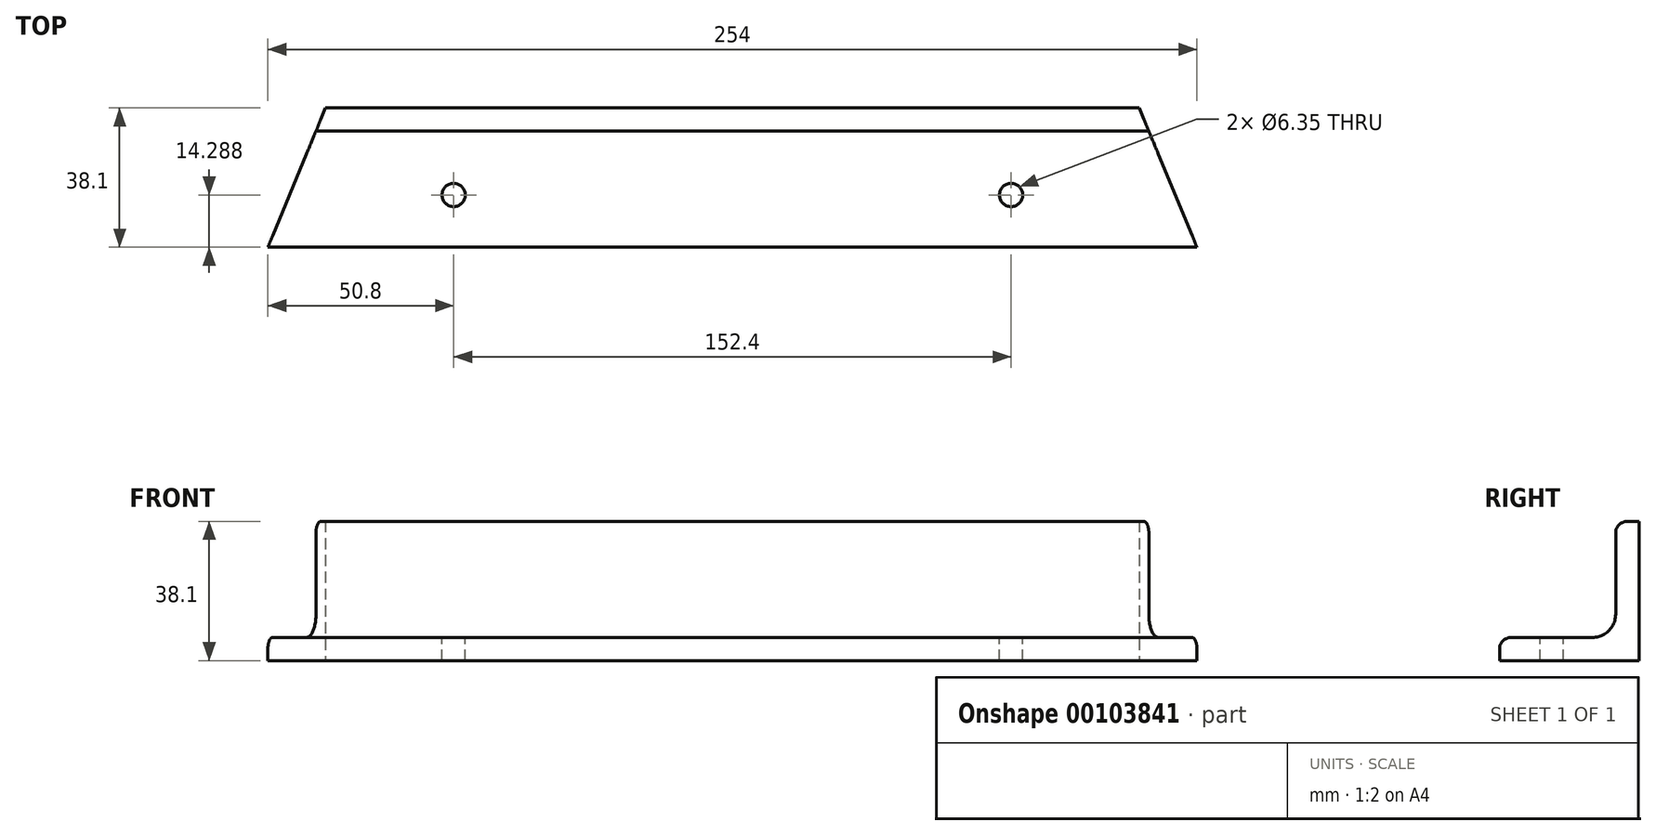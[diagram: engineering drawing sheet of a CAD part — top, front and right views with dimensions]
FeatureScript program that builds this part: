
annotation { "Feature Type Name" : "Feature", "Feature Type Description" : "" }
export const myFeature = defineFeature(function(context is Context, id is Id, definition is map)
    precondition{}
    {
        {
            var Q0;
            Q0=qCreatedBy(makeId("Right.planeOp"),FACE);
            var sketch = newSketch(context, id + "F0", { "sketchPlane" : qUnion([Q0])});
            skLineSegment(sketch, "E0", {"start": v(0, 0) * mm, "end": v(0, 38.1) * mm});
            skLineSegment(sketch, "E1", {"start": v(0, 38.1) * mm, "end": v(-6.35, 38.1) * mm});
            skLineSegment(sketch, "E2", {"start": v(-6.35, 38.1) * mm, "end": v(-6.35, 6.35) * mm});
            skLineSegment(sketch, "E3", {"start": v(-6.35, 6.35) * mm, "end": v(-38.1, 6.35) * mm});
            skLineSegment(sketch, "E4", {"start": v(-38.1, 6.35) * mm, "end": v(-38.1, 0) * mm});
            skLineSegment(sketch, "E5", {"start": v(-38.1, 0) * mm, "end": v(0, 0) * mm});
            skSolve(sketch);
        }
        {
            var Q0;
            Q0 = qSketchRegion(id + "F0", true);
            extrude(context, id + "F1", {"entities" : qUnion([Q0]), "endBound" : BoundingType.SYMMETRIC, "depth" : 254 * mm});
        }
        {
            var Q0;
            Q0=makeQuery(id+"F1.opExtrude","SWEPT_EDGE",EDGE,{"disambiguationData":[OSD([sQuery(id+"F0.wireOp",EDGE,"E2"),sQuery(id+"F0.wireOp",EDGE,"E3")])]});
            fillet(context, id + "F2", {"entities" : qUnion([Q0]), "radius" : 6.35 * mm, "tangentPropagation" : true, "allowEdgeOverflow" : false});
        }
        {
            var Q0;
            Q0=makeQuery(id+"F1.opExtrude","SWEPT_EDGE",EDGE,{"disambiguationData":[OSD([sQuery(id+"F0.wireOp",EDGE,"E1"),sQuery(id+"F0.wireOp",EDGE,"E2")])]});
            var Q1;
            Q1=makeQuery(id+"F1.opExtrude","SWEPT_EDGE",EDGE,{"disambiguationData":[OSD([sQuery(id+"F0.wireOp",EDGE,"E3"),sQuery(id+"F0.wireOp",EDGE,"E4")])]});
            fillet(context, id + "F3", {"entities" : qUnion([Q0, Q1]), "radius" : 3.17 * mm, "tangentPropagation" : true, "allowEdgeOverflow" : false});
        }
        {
            var Q0;
            Q0=makeQuery(id+"F1.opExtrude","SWEPT_FACE",FACE,{"disambiguationData":[OSD([sQuery(id+"F0.wireOp",EDGE,"E3")])]});
            var sketch = newSketch(context, id + "F4", { "sketchPlane" : qUnion([Q0])});
            skCircle(sketch, "E6", {"center": v(-76.2, -23.81) * mm, "radius": 3.18 * mm});
            skCircle(sketch, "E7", {"center": v(76.2, -23.81) * mm, "radius": 3.18 * mm});
            skLineSegment(sketch, "E8", {"start": v(-127, -23.81) * mm, "end": v(-76.2, -23.81) * mm, "construction": true});
            skLineSegment(sketch, "E9", {"start": v(127, -23.81) * mm, "end": v(76.2, -23.81) * mm, "construction": true});
            skSolve(sketch);
        }
        {
            var Q0;
            Q0 = qSketchRegion(id + "F4", true);
            extrude(context, id + "F5", {"entities" : qUnion([Q0]), "operationType" : NewBodyOperationType.REMOVE, "endBound" : BoundingType.THROUGH_ALL, "oppositeDirection" : true, "depth" : 25.4 * mm});
        }
        {
            var Q0;
            Q0=makeQuery(id+"F1.opExtrude","SWEPT_FACE",FACE,{"disambiguationData":[OSD([sQuery(id+"F0.wireOp",EDGE,"E5")])]});
            var sketch = newSketch(context, id + "F6", { "sketchPlane" : qUnion([Q0])});
            skLineSegment(sketch, "E10", {"start": v(-127, 38.1) * mm, "end": v(-127, 0) * mm});
            skLineSegment(sketch, "E11", {"start": v(-127, 0) * mm, "end": v(-111.22, 0) * mm});
            skLineSegment(sketch, "E12", {"start": v(-111.22, 0) * mm, "end": v(-127, 38.1) * mm});
            skLineSegment(sketch, "E13", {"start": v(0, 0) * mm, "end": v(0, 38.1) * mm, "construction": true});
            skLineSegment(sketch, "E14.MirrorCS", {"start": v(127, 0) * mm, "end": v(111.22, 0) * mm});
            skLineSegment(sketch, "E15.MirrorCS", {"start": v(127, 38.1) * mm, "end": v(127, 0) * mm});
            skLineSegment(sketch, "E16.MirrorCS", {"start": v(111.22, 0) * mm, "end": v(127, 38.1) * mm});
            skSolve(sketch);
        }
        {
            var Q0;
            Q0 = qSketchRegion(id + "F6", true);
            extrude(context, id + "F7", {"entities" : qUnion([Q0]), "operationType" : NewBodyOperationType.REMOVE, "endBound" : BoundingType.THROUGH_ALL, "oppositeDirection" : true, "depth" : 25.4 * mm});
        }
    });
